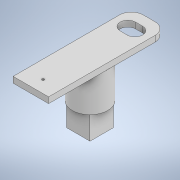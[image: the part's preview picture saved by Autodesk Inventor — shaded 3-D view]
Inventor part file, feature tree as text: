
AUTODESK INVENTOR PART (.ipt)
format: ipt  version: 2022.3 (Build 263350000, 350)  size: 141,824 bytes
history: native  units: in
note: dims shown in document units (in); Inventor stores cm internally (conversion verified against a paired STEP export)
features: extrude x5, sketch x5, fillet x1
ambient origin geometry x8: Origin, YZ Plane, XZ Plane, XY Plane, X Axis, Y Axis, Z Axis, Center Point
bodies: Solid1 (feature_tree)
feature tree (11):
  extrude  "Extrusion1"  Depth=0.7874in
  extrude  "Extrusion2"  Depth=1.1811in
  extrude  "Extrusion3"  Depth=1.1811in
  extrude  "Extrusion4"  Depth=0.1969in TaperAngle=0.0deg
  fillet  "Fillet1"  Radius=0.5118in
  extrude  "Extrusion5"  Depth=0.1969in
  sketch  "Sketch1"  dims[d0=0.7874in d1=0.7874in]
  sketch  "Sketch2"  dims[d2=0.7874in d3=0.0in d4=1.1811in]
  sketch  "Sketch3"  dims[d5=1.1811in d6=0.0in d7=1.1811in]
  sketch  "Sketch4"  dims[d8=3.937in d9=0.1969in d10=0.0in d11=0.5118in]
  sketch  "Sketch5"  dims[d12=0.5118in d13=0.1181in d14=0.1181in d15=1.378in d16=0.1969in d17=0.0in d18=0.3937in d19=0.0787in d20=0.1969in d21=0.0in]
